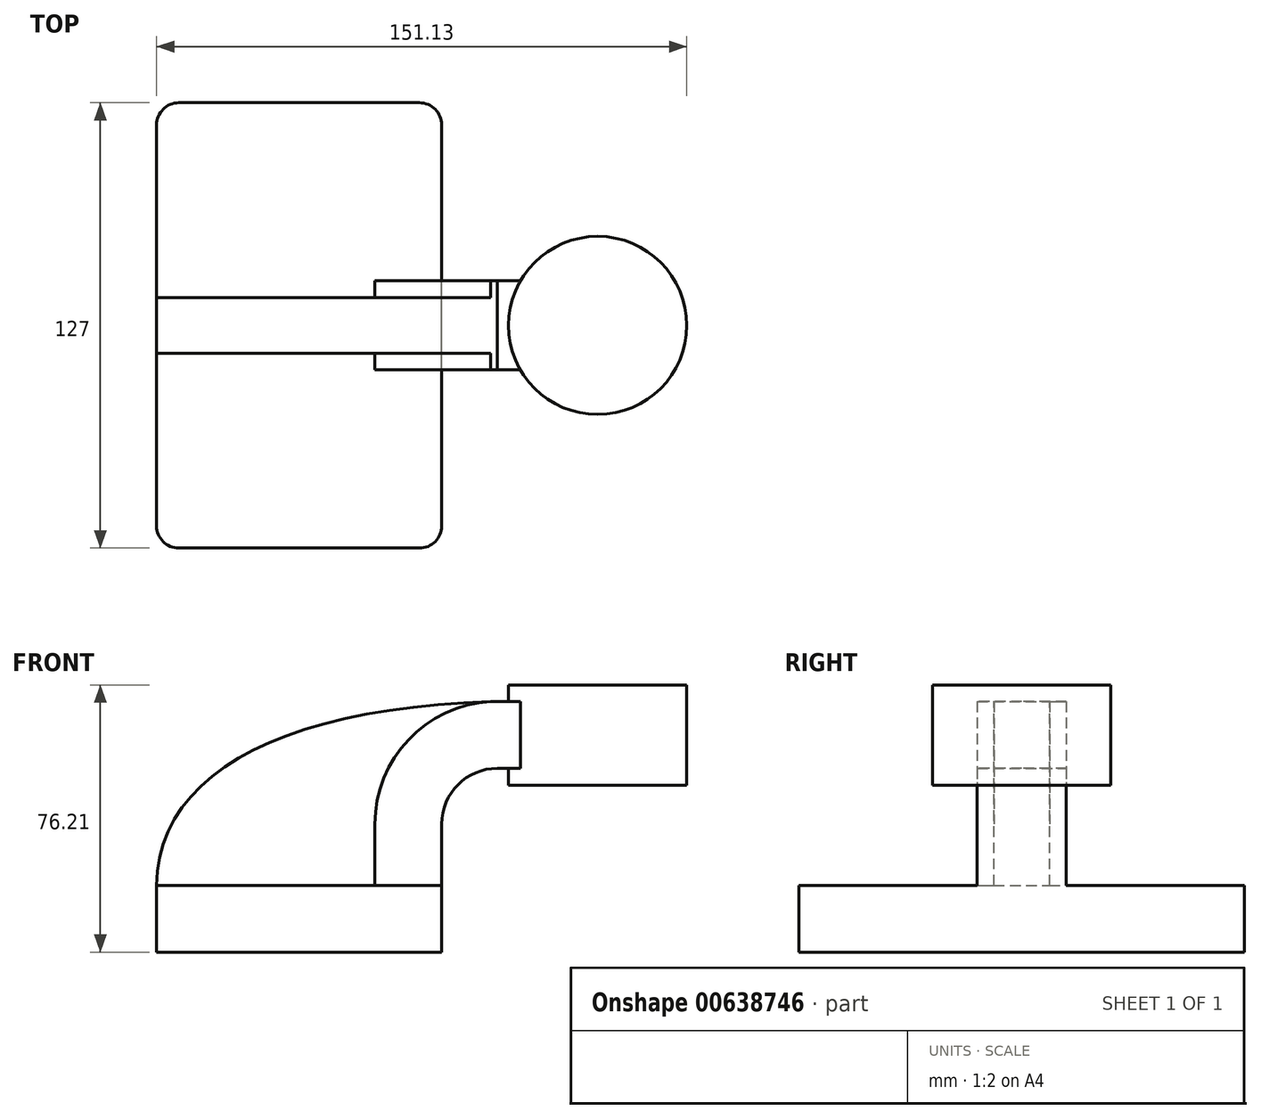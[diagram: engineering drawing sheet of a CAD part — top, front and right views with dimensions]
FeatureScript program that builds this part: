
annotation { "Feature Type Name" : "Feature", "Feature Type Description" : "" }
export const myFeature = defineFeature(function(context is Context, id is Id, definition is map)
    precondition{}
    {
        {
            var Q0;
            Q0=qCreatedBy(makeId("Front.planeOp"),FACE);
            var sketch = newSketch(context, id + "F0", { "sketchPlane" : qUnion([Q0])});
            skLineSegment(sketch, "E0.bottom", {"start": v(40.64, 9.53) * mm, "end": v(-40.64, 9.53) * mm});
            skLineSegment(sketch, "E0.top", {"start": v(40.64, -9.52) * mm, "end": v(-40.64, -9.52) * mm});
            skLineSegment(sketch, "E0.left", {"start": v(40.64, 9.53) * mm, "end": v(40.64, -9.52) * mm});
            skLineSegment(sketch, "E0.right", {"start": v(-40.64, 9.53) * mm, "end": v(-40.64, -9.52) * mm});
            skPoint(sketch, "E0.middle", {"position": v(0, 0) * mm});
            skLineSegment(sketch, "E1.bottom", {"start": v(59.7, 38.1) * mm, "end": v(110.5, 38.1) * mm});
            skLineSegment(sketch, "E1.top", {"start": v(59.7, 66.68) * mm, "end": v(110.5, 66.68) * mm});
            skLineSegment(sketch, "E1.left", {"start": v(59.7, 38.1) * mm, "end": v(59.69, 66.68) * mm});
            skLineSegment(sketch, "E1.right", {"start": v(110.5, 38.1) * mm, "end": v(110.5, 66.68) * mm});
            skPoint(sketch, "E1.middle", {"position": v(85.1, 52.39) * mm});
            skLineSegment(sketch, "E2", {"start": v(40.64, 9.53) * mm, "end": v(40.64, 27) * mm});
            skArc(sketch, "E3", {"start": v(40.64, 27) * mm, "mid": v(45.29, 38.23) * mm, "end": v(56.51, 42.88) * mm});
            skLineSegment(sketch, "E4", {"start": v(56.51, 42.88) * mm, "end": v(85.1, 42.88) * mm});
            skPoint(sketch, "E4.endSnap0", {"position": v(85.1, 38.1) * mm});
            skLineSegment(sketch, "E5.0", {"start": v(56.52, 61.93) * mm, "end": v(85.1, 61.93) * mm});
            skArc(sketch, "E5.1", {"start": v(21.59, 27) * mm, "mid": v(31.82, 51.7) * mm, "end": v(56.52, 61.93) * mm});
            skLineSegment(sketch, "E5.2", {"start": v(21.59, 9.53) * mm, "end": v(21.59, 27) * mm});
            skLineSegment(sketch, "E6", {"start": v(85.1, 38.1) * mm, "end": v(85.1, 66.68) * mm});
            skFitSpline(sketch, "E7", {"points": [v(-40.64, 9.53) * mm, v(56.51, 61.93) * mm], "startDerivative": vector(1.13, 96.19) * mm, "endDerivative": vector(182.29, 4.37) * mm});
            skSolve(sketch);
        }
        {
            var Q0;
            Q0=makeQuery(id+"F0.imprint","IMPRINT",FACE,{"disambiguationData":[TD([[makeQuery(id+"F0.imprint","IMPRINT",EDGE,{"derivedFrom":sQuery(id+"F0.wireOp",EDGE,"E0.top")}),-1.0]])]});
            extrude(context, id + "F1", {"entities" : qUnion([Q0]), "endBound" : BoundingType.SYMMETRIC, "depth" : 127 * mm, "offsetDistance" : 25.4 * mm});
        }
        {
            var Q0;
            {var subQ1=sQuery(id+"F0.wireOp",EDGE,"E2");Q0=makeQuery(id+"F0.imprint","IMPRINT",FACE,{"disambiguationData":[TD([[makeQuery(id+"F0.imprint","IMPRINT",EDGE,{"derivedFrom":subQ1}),1.0]])]});}
            var Q1;
            {var subQ0=sQuery(id+"F0.wireOp",EDGE,"E4");var subQ1=sQuery(id+"F0.wireOp",EDGE,"E1.left");var subQ2=makeQuery(id+"F0.imprint","INTERSECT",VERTEX,{"derivedFrom":[subQ1,subQ0]});Q1=makeQuery(id+"F0.imprint","IMPRINT",FACE,{"disambiguationData":[TD([[makeQuery(id+"F0.imprint","IMPRINT",EDGE,{"disambiguationData":[TD([[subQ2,-1.0]])],"derivedFrom":subQ1}),-1.0]])]});}
            extrude(context, id + "F2", {"entities" : qUnion([Q0, Q1]), "operationType" : NewBodyOperationType.ADD, "endBound" : BoundingType.SYMMETRIC, "depth" : 25.4 * mm, "offsetDistance" : 25.4 * mm});
        }
        {
            var Q0;
            {var subQ3=sQuery(id+"F0.wireOp",EDGE,"E5.2");Q0=makeQuery(id+"F0.imprint","IMPRINT",FACE,{"disambiguationData":[TD([[makeQuery(id+"F0.imprint","IMPRINT",EDGE,{"derivedFrom":subQ3}),1.0]])]});}
            extrude(context, id + "F3", {"entities" : qUnion([Q0]), "operationType" : NewBodyOperationType.ADD, "endBound" : BoundingType.SYMMETRIC, "depth" : 15.88 * mm, "offsetDistance" : 25.4 * mm});
        }
        {
            var Q0;
            {var subQ4=sQuery(id+"F0.wireOp",EDGE,"E1.right");Q0=makeQuery(id+"F0.imprint","IMPRINT",FACE,{"disambiguationData":[TD([[makeQuery(id+"F0.imprint","IMPRINT",EDGE,{"derivedFrom":subQ4}),1.0]])]});}
            var Q1;
            Q1=sQuery(id+"F0.wireOp",EDGE,"E6");
            revolve(context, id + "F4", {"operationType" : NewBodyOperationType.ADD, "entities" : qUnion([Q0]), "axis" : qUnion([Q1]), "revolveType" : RevolveType.FULL});
        }
        {
            var Q0;
            Q0=makeQuery(id+"F1.opExtrude","CAP_EDGE",EDGE,{"disambiguationData":[OSD([sQuery(id+"F0.wireOp",EDGE,"E0.left")])],"isStart":false});
            fillet(context, id + "F5", {"entities" : qUnion([Q0]), "radius" : 6.35 * mm, "tangentPropagation" : true, "allowEdgeOverflow" : false});
        }
        {
            var Q0;
            Q0=makeQuery(id+"F1.opExtrude","CAP_EDGE",EDGE,{"disambiguationData":[OSD([sQuery(id+"F0.wireOp",EDGE,"E0.right")])],"isStart":false});
            fillet(context, id + "F6", {"entities" : qUnion([Q0]), "radius" : 6.35 * mm, "tangentPropagation" : true, "allowEdgeOverflow" : false});
        }
        {
            var Q0;
            Q0=makeQuery(id+"F1.opExtrude","CAP_EDGE",EDGE,{"disambiguationData":[OSD([sQuery(id+"F0.wireOp",EDGE,"E0.left")])],"isStart":true});
            var Q1;
            Q1=makeQuery(id+"F1.opExtrude","CAP_EDGE",EDGE,{"disambiguationData":[OSD([sQuery(id+"F0.wireOp",EDGE,"E0.right")])],"isStart":true});
            fillet(context, id + "F7", {"entities" : qUnion([Q0, Q1]), "radius" : 6.35 * mm, "tangentPropagation" : true, "allowEdgeOverflow" : false});
        }
    });
